# Revit family: 2CKA006800A2520
name_source: partatom
category: Elektroinstallationen
revit_build: Autodesk Revit 2017 (Build: 20160225_1515(x64)
units: mm (PartAtom-declared; Revit-internal decimal feet)

## family parameters
Basisbauteil = Fläche
Beim Laden mit Abzugskörper schneiden = Nein
Bemaßung runder Anschluss = Durchmesser verwenden
Beschriftungsausrichtung beibehalten = Nein
Gemeinsam genutzt = Nein
Raumberechnungspunkt = Nein
Teiletyp = Normal

## types (1)
- 2CKA006800A2520
    Ansprechempfindlichkeit einstellbar = Ja
    Ansprechhelligkeit [lx] = [0,5:1000]
    Ansprechhelligkeit einstellbar = Ja
    Ausführung = Bewegungsmelder
    Ausführung der Oberfläche = matt
    BIM = https://media.live.bim.site
    BIMSITE_PRODUCT_ID = 9e1ec58d990c495361cd790bfc85e80c28fad2a2
    Beschreibung = Busch-Wächter 220 MasterLINE, alpinweiß, Bewegungs-/Präsenzmelder, Busch-Wächter AP, Busch-Wächter 220 MasterLINE Elektronischer Bewegungsmelder zur Erkennung von Wärmebewegungen. Fernbedienbar über IR Handsender 6841-101. Fernparametrierbar über IR Service-Handsender 6842-101. Mit Erfassungs- und Betriebsartenanzeige. Mit Boden- und Rückfeldüberwachung. Mit Profilinse für beste Erfassung. Erfassungsempfindlichkeit über IR Service-Handsender einstellbar. Überwachungsdichte: 84 Sektoren mit 336 Schaltsegmenten. Mit integrierter Demontageerschwernis. Alle Funktionen mikroprozessorgesteuert. Dauerlicht (4 Std.), Lichtausschaltung (4 Std.) und Anwesenheitssimulation über IR Handsender aktivierbar. Einlesen des aktuellen Helligkeitswertes als Schaltschwelle über IR Handsender. Mit automatischer Reichweitenstabilisierung. Mit automatischer Störunterdrückung. Mit automatischer Blendsicherheit. Mit helligkeitsunabhängigem Testbetrieb zur Auswertung des Erfassungsbereiches. Individuelle Anpassung des Erfassungsbereiches über beiliegende, zuschneidbare Abdeckfolie. Zusätzliche Einschaltmöglichkeit über Öffnertaster. Abschaltverzögerung: 10 s bis 30 min oder Kurzzeitimpuls 1 s einstellbar. Nennspannung: , +10 % / -10 % Nennfrequenz: 50 Hz/60 Hz Ausgänge: 1x Schließer, potenzialgebunden Lastart: ohmisch, kapazitiv und induktiv Nennstrom: 16 AX, bei cos ? 0,6 Nennleistung: 3680 W/VA Erfassungsbereich: frontal: 16 m, seitlich: 16 m Öffnungswinkel: 220 ° Helligkeitsgrenzwert: 0,5 Lux - 300 Lux , Tagbetrieb Montagehöhe: 2,5 m Schutzart Gerät: IP 55 Temperaturbereich Gerät: -25 °C bis 55 °C Maße (H x B x T): 115 mm x 125 mm x 141 mm
    Datenblatt = https://media.live.bim.site
    Erfassungsfeld Durchmesser auf Fußboden [m] = 32
    Erfassungswinkel horizontal [°] = [8:220]
    Farbe = weiß
    Fernbedienbar = Ja
    Frequenz [Hz] = [50:60]
    GTIN = 4011395150511
    Gerätebreite [mm] = 125
    Gerätehöhe [mm] = 115
    Gerätetiefe [mm] = 135
    Gewicht [kg/m] = 0.343
    HAN = 2CKA006800A2520
    Halogenfrei = Ja
    HeinzeBIM = https://www.heinze.de
    Hersteller = Busch-Jaeger
    Ist System = Nein
    Ist Zubehör = Nein
    Konstantlichtregelung = Nein
    Max. Einschaltdauer [s] = 1800
    Max. Einschaltstrom = 80 A
    Max. Reichweite frontal [m] = 16
    Max. Reichweite zu einer Seite [m] = 16
    Max. Schaltleistung [Voltampere] = 3680
    Min. Einschaltdauer [s] = 10
    Montageart = Aufputz
    Nebenstelleneingang = Nein
    Nennspannung [V] [Volt] = 230
    Oberfläche = unbehandelt
    Produktseite = https://media.live.bim.site
    RAL-Nummer (ähnlich) = 9010
    Schutzart (IP) = IP55
    TYPE = 6847/11 AGM-204
    Teach-Funktion für Ansprechhelligkeit = Ja
    Temperatur [K] = [-25:55]
    Treppenhausüberwachung = Ja
    Typname = Busch-Wächter 220 MasterLINE, alpinweiß, Bewegungs-/Präsenzmelder, Busch-Wächter AP
    URL = https://www.busch-jaeger.de
    Unterkriechschutz/Rückfeldüberwachung = Ja
    Vorgabe-Ansicht = 1219 mm
    Werkstoff = Kunststoff
    Werkstoffgüte = Thermoplast
    Zwangsabschaltung = Ja

## geometry (parser evidence)
native form markers: Sweep x3
no freeform markers — native parametric forms only
